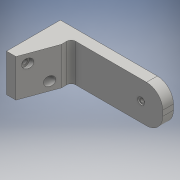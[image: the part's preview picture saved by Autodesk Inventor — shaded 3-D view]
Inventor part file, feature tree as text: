
AUTODESK INVENTOR PART (.ipt)
format: ipt  version: 2016 (Build 200138000, 138)  size: 165,376 bytes
history: native  units: mm
features: sketch x8, extrude x5, hole x3, fillet x3, plane x1
ambient origin geometry x8: Origin, YZ Plane, XZ Plane, XY Plane, X Axis, Y Axis, Z Axis, Center Point
bodies: Solid1 (feature_tree)
feature tree (20):
  extrude  "Extrusion1"  Depth=105.0mm
  extrude  "Extrusion2"  Depth=10.0mm
  hole  "Hole1"  [1 undecoded]
  extrude  "Extrusion3"  Depth=20.0mm
  extrude  "Extrusion4"  Depth=40.0mm TaperAngle=0.0deg
  plane  "Work Plane1"
  extrude  "Extrusion5"  Depth=8.5mm
  hole  "Hole2"  [1 undecoded]
  hole  "Hole3"  [1 undecoded]
  fillet  "Fillet1"  Radius=8.0mm
  fillet  "Fillet2"  Radius=8.0mm
  fillet  "Fillet3"  Radius=11.0mm
  sketch  "Sketch1"  dims[d0=35.0mm d1=105.0mm]
  sketch  "Sketch2"  dims[d2=10.0mm d3=0.0mm d4=22.5mm]
  sketch  "Sketch3"  dims[d5=17.5mm d6=85.0mm]
  sketch  "Sketch4"  dims[d7=5.0mm d8=0.0mm]
  sketch  "Sketch5"  dims[d9=4.0mm d10=6.0mm d11=6.5mm d12=1.0mm d13=90.0deg d14=8.0mm d15=20.594885mm d16=20.0mm]
  sketch  "Sketch6"  dims[d17=40.0mm d18=0.0mm d19=42.0mm d20=0.0mm]
  sketch  "Sketch7"  dims[d21=-20.0mm d22=8.5mm]
  sketch  "Sketch8"  dims[d23=8.0mm d24=8.0mm d25=8.5mm d26=8.0mm d27=8.0mm d28=11.0mm d29=0.0mm d30=4.5mm d31=6.0mm d32=6.5mm d33=1.0mm d34=90.0deg d35=10.0mm d36=20.594885mm d37=4.5mm d38=6.0mm d39=6.5mm d40=1.0mm d41=90.0deg d42=10.0mm d43=20.594885mm d44=4.0mm d45=15.0mm d46=15.0mm]
note: 3 required parameter values undecoded (feature->parameter linkage not recoverable at this tier; creation-order binding heuristic only, values carry confidence <= 0.55)
